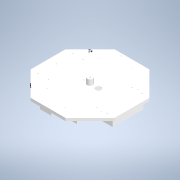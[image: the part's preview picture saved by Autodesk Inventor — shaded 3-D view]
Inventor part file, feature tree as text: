
AUTODESK INVENTOR PART (.ipt)
format: ipt  version: 2020.2 (Build 242310000, 310)  size: 401,408 bytes
history: native  units: in
note: dims shown in document units (in); Inventor stores cm internally (conversion verified against a paired STEP export)
features: sketch x22, extrude x15, hole x5, shell x1
ambient origin geometry x8: Origin, YZ Plane, XZ Plane, XY Plane, X Axis, Y Axis, Z Axis, Center Point
bodies: Solid1 (feature_tree)
feature tree (43):
  extrude  "Extrusion1"  Depth=0.3937in TaperAngle=0.0deg
  extrude  "Extrusion2"  Depth=0.1575in
  extrude  "Extrusion3"  Depth=0.7874in
  extrude  "Extrusion4"  Depth=0.7874in TaperAngle=0.0deg
  shell  "Shell1"  Thickness=11.9291in
  extrude  "Extrusion5"  Depth=4.3307in
  hole  "Hole1"  [1 undecoded]
  extrude  "Extrusion6"  Depth=3.937in
  hole  "Hole2"  [1 undecoded]
  hole  "Hole3"  [1 undecoded]
  hole  "Hole4"  [1 undecoded]
  hole  "Hole5"  [1 undecoded]
  extrude  "Extrusion7"  Depth=1.4961in
  extrude  "Extrusion8"  Depth=1.4961in
  extrude  "Extrusion9"  Depth=1.9685in TaperAngle=0.0deg
  extrude  "Extrusion10"  Depth=0.7874in
  extrude  "Extrusion11"  Depth=0.6398in TaperAngle=0.0deg
  sketch  "Sketch17"  dims[d45=0.3937in d46=0.2953in d47=0.1476in d48=0.0984in d49=90.0deg d50=1.1811in d51=0.0in]
  sketch  "Sketch18"  dims[d52=0.3937in d53=0.2953in d54=0.1476in d55=0.0984in d56=90.0deg d57=0.1181in d58=0.0in]
  extrude  "Extrusion12"  Depth=0.5315in
  extrude  "Extrusion13"  Depth=0.5315in
  extrude  "Extrusion14"  Depth=0.7874in
  extrude  "Extrusion15"  Depth=0.3937in TaperAngle=0.0deg
  sketch  "Sketch1"  dims[d0=11.9291in d1=0.3937in d2=0.0in]
  sketch  "Sketch2"  dims[d3=0.1575in d4=0.1575in]
  sketch  "Sketch3"  dims[d5=1.1811in d6=0.0in d7=0.7874in]
  sketch  "Sketch4"  dims[d8=0.1969in d9=0.7874in d10=0.0in d11=11.9291in]
  sketch  "Sketch5"  dims[d12=2.3622in d13=4.3307in]
  sketch  "Sketch6"  dims[d14=2.5591in d15=8.6614in]
  sketch  "Sketch7"  dims[d16=3.937in d17=3.937in]
  sketch  "Sketch8"  dims[d18=1.5748in d19=2.9528in]
  sketch  "Sketch9"  dims[d20=2.9528in d21=1.9685in d22=0.0in]
  sketch  "Sketch10"  dims[d23=0.0394in d24=2.2835in]
  sketch  "Sketch11"  dims[d25=4.252in d26=3.8583in]
  sketch  "Sketch12"  dims[d27=3.8583in d28=1.4961in]
  sketch  "Sketch13"  dims[d29=2.874in d30=1.4961in]
  sketch  "Sketch14"  dims[d31=2.874in d32=1.9685in d33=0.0in]
  sketch  "Sketch15"  dims[d34=0.7874in d35=0.2953in d36=0.1476in d37=0.0984in d38=90.0deg d39=1.1811in d40=0.0in d41=0.7874in]
  sketch  "Sketch16"  dims[d42=0.8661in d43=0.6398in d44=0.0in]
  sketch  "Sketch19"  dims[d59=0.4921in d60=0.2953in d61=0.1476in d62=0.0984in d63=90.0deg d64=1.1811in d65=0.0in]
  sketch  "Sketch20"  dims[d66=0.4921in d67=0.2953in d68=0.1476in d69=0.0984in d70=90.0deg d71=1.1811in d72=0.0in d73=0.5315in]
  sketch  "Sketch21"  dims[d74=0.2756in d75=0.0in d76=0.5315in]
  sketch  "Sketch22"  dims[d77=0.2756in d78=0.0in d79=0.7874in d80=0.3937in d81=0.0in d82=0.4331in d83=0.4331in d84=0.374in d85=0.0in d86=0.7874in d87=0.0in d88=0.3937in d89=0.3937in d90=0.1575in d91=0.1575in d92=0.1575in d93=0.1575in d94=0.1575in d95=0.1575in d96=0.3937in d97=0.0in d98=0.7874in d99=0.0in d100=0.0787in d101=0.0in d102=0.1575in d103=0.1575in d104=0.1575in d105=0.1575in d106=0.3937in d107=0.0in]
note: 5 required parameter values undecoded (feature->parameter linkage not recoverable at this tier; creation-order binding heuristic only, values carry confidence <= 0.55)
